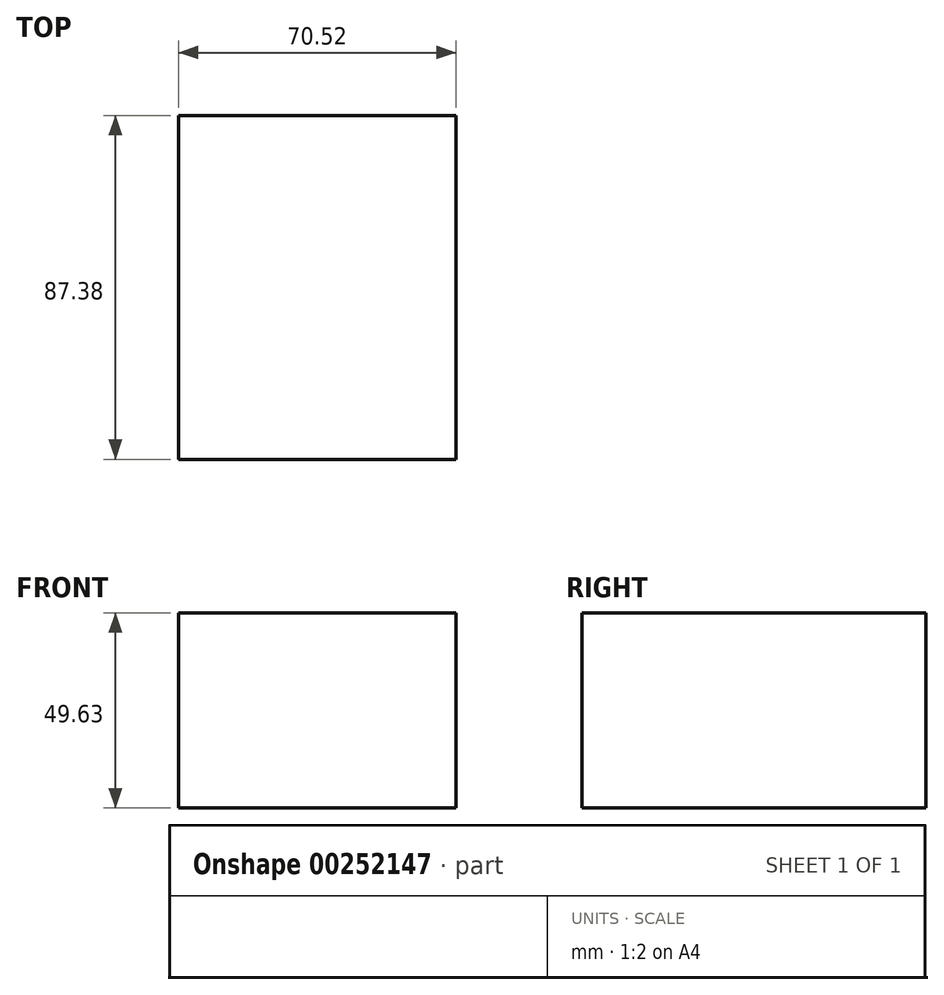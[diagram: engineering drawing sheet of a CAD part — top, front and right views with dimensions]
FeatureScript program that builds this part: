
annotation { "Feature Type Name" : "Feature", "Feature Type Description" : "" }
export const myFeature = defineFeature(function(context is Context, id is Id, definition is map)
    precondition{}
    {
        {
            var Q0;
            Q0=qCreatedBy(makeId("Front.planeOp"),FACE);
            var sketch = newSketch(context, id + "F0", { "sketchPlane" : qUnion([Q0])});
            skLineSegment(sketch, "E0.bottom", {"start": v(-25.82, 22.56) * mm, "end": v(-96.34, 22.56) * mm});
            skLineSegment(sketch, "E0.top", {"start": v(-25.82, -27.07) * mm, "end": v(-96.34, -27.07) * mm});
            skLineSegment(sketch, "E0.left", {"start": v(-25.82, 22.56) * mm, "end": v(-25.82, -27.07) * mm});
            skLineSegment(sketch, "E0.right", {"start": v(-96.34, 22.56) * mm, "end": v(-96.34, -27.07) * mm});
            skPoint(sketch, "E0.middle", {"position": v(-61.08, -2.25) * mm});
            skSolve(sketch);
        }
        {
            var Q0;
            Q0 = qSketchRegion(id + "F0", true);
            extrude(context, id + "F1", {"entities" : qUnion([Q0]), "depth" : 87.38 * mm});
        }
    });
